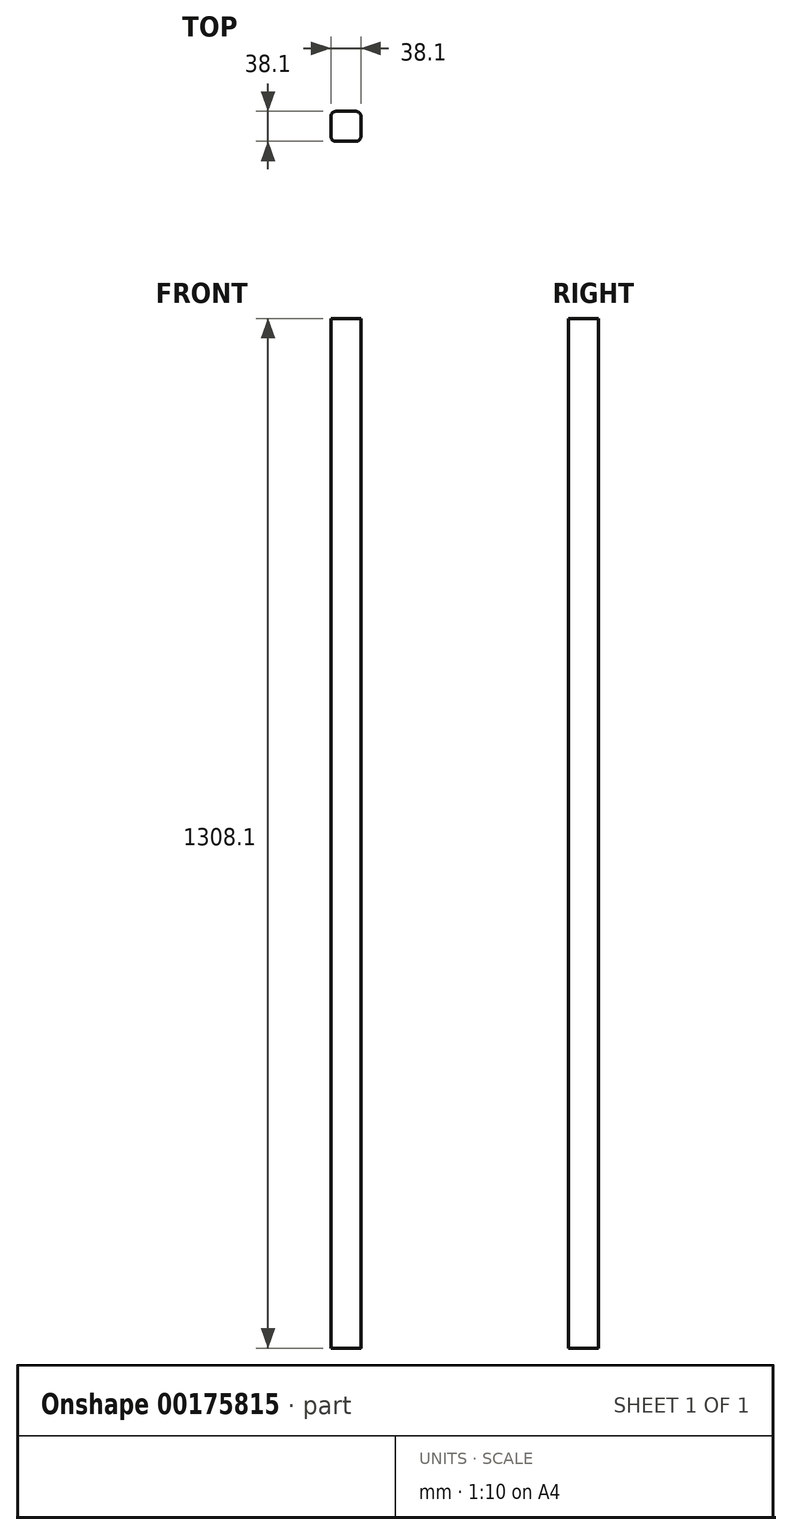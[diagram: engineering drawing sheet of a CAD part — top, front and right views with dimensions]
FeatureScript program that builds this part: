
annotation { "Feature Type Name" : "Feature", "Feature Type Description" : "" }
export const myFeature = defineFeature(function(context is Context, id is Id, definition is map)
    precondition{}
    {
        {
            var Q0;
            Q0=qCreatedBy(makeId("Top.planeOp"),FACE);
            var sketch = newSketch(context, id + "F0", { "sketchPlane" : qUnion([Q0])});
            skLineSegment(sketch, "E0.bottom", {"start": v(12.7, 19.05) * mm, "end": v(-12.7, 19.05) * mm});
            skLineSegment(sketch, "E0.top", {"start": v(12.7, -19.05) * mm, "end": v(-12.7, -19.05) * mm});
            skLineSegment(sketch, "E0.left", {"start": v(19.05, 12.7) * mm, "end": v(19.05, -12.7) * mm});
            skLineSegment(sketch, "E0.right", {"start": v(-19.05, 12.7) * mm, "end": v(-19.05, -12.7) * mm});
            skPoint(sketch, "E0.middle", {"position": v(0, 0) * mm});
            skPoint(sketch, "E1.visualSharp", {"position": v(-19.05, 19.05) * mm});
            skArc(sketch, "E1.filletArc", {"start": v(-12.7, 19.05) * mm, "mid": v(-17.2, 17.2) * mm, "end": v(-19.05, 12.7) * mm});
            skPoint(sketch, "E2.visualSharp", {"position": v(19.05, 19.05) * mm});
            skArc(sketch, "E2.filletArc", {"start": v(19.05, 12.7) * mm, "mid": v(17.2, 17.2) * mm, "end": v(12.7, 19.05) * mm});
            skPoint(sketch, "E3.visualSharp", {"position": v(19.05, -19.05) * mm});
            skArc(sketch, "E3.filletArc", {"start": v(12.7, -19.05) * mm, "mid": v(17.2, -17.2) * mm, "end": v(19.05, -12.7) * mm});
            skPoint(sketch, "E4.visualSharp", {"position": v(-19.05, -19.05) * mm});
            skArc(sketch, "E4.filletArc", {"start": v(-19.05, -12.7) * mm, "mid": v(-17.2, -17.2) * mm, "end": v(-12.7, -19.05) * mm});
            skSolve(sketch);
        }
        {
            var Q0;
            Q0=qSketchRegion(id+"F0",true);
            extrude(context, id + "F1", {"entities" : qUnion([Q0]), "depth" : 1308.1 * mm, "offsetDistance" : 25.4 * mm});
        }
    });
